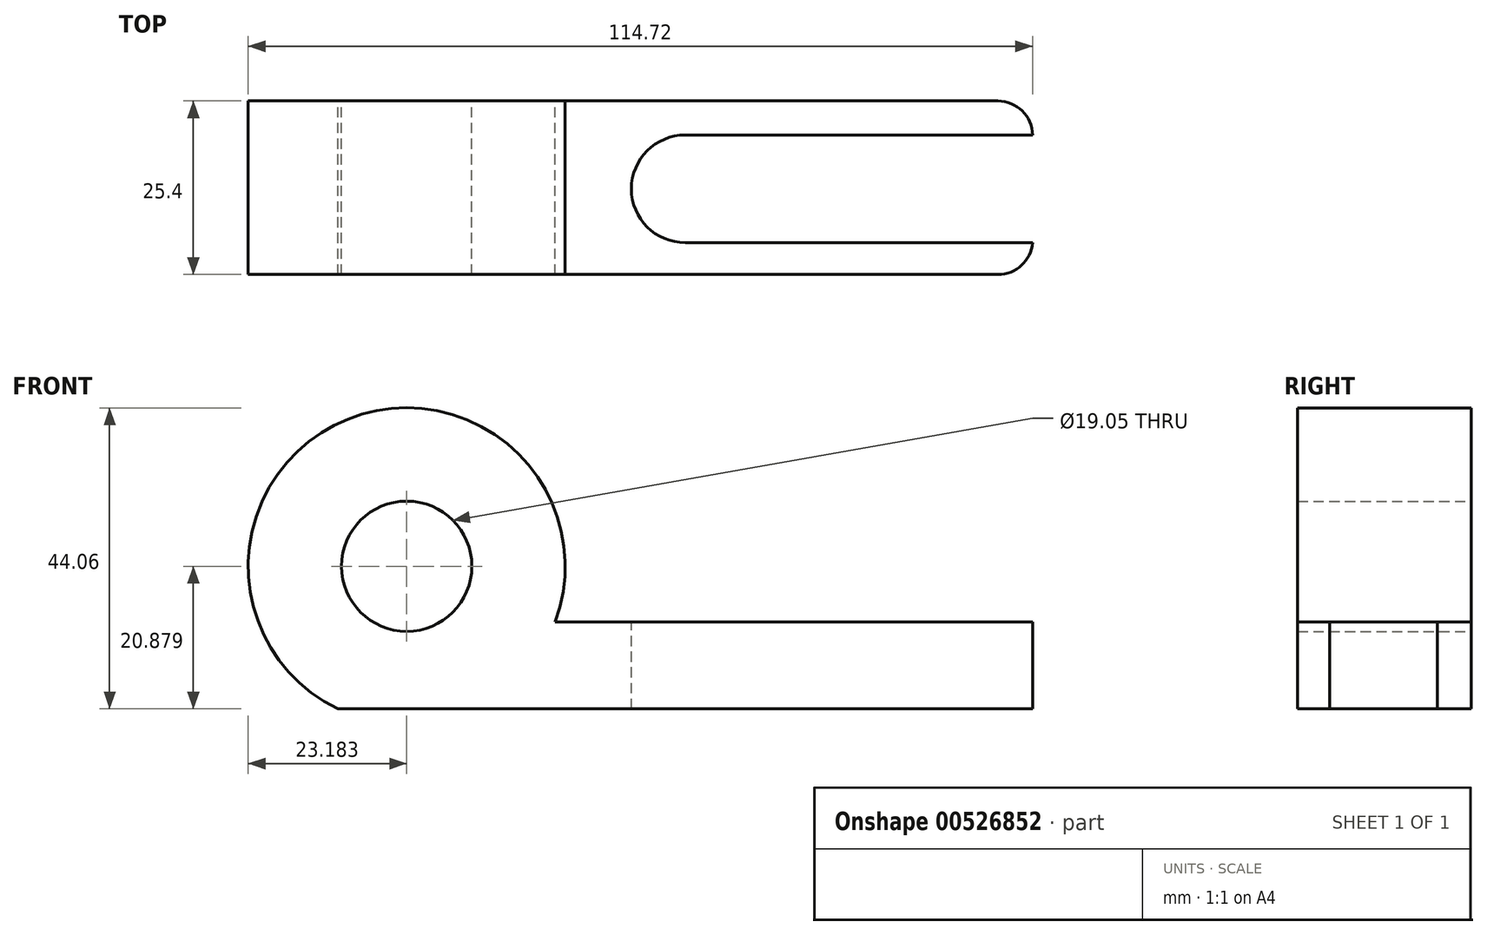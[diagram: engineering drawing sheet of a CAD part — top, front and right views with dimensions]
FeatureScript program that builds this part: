
annotation { "Feature Type Name" : "Feature", "Feature Type Description" : "" }
export const myFeature = defineFeature(function(context is Context, id is Id, definition is map)
    precondition{}
    {
        {
            var Q0;
            Q0=qCreatedBy(makeId("Front.planeOp"),FACE);
            var sketch = newSketch(context, id + "F0", { "sketchPlane" : qUnion([Q0])});
            skLineSegment(sketch, "E0", {"start": v(-52.73, 0) * mm, "end": v(48.87, 0) * mm});
            skLineSegment(sketch, "E1", {"start": v(48.87, 0) * mm, "end": v(48.87, 12.7) * mm});
            skLineSegment(sketch, "E2", {"start": v(48.87, 12.7) * mm, "end": v(-20.98, 12.7) * mm});
            skArc(sketch, "E3", {"start": v(-20.98, 12.7) * mm, "mid": v(-51.28, 42.4) * mm, "end": v(-52.73, 0) * mm});
            skCircle(sketch, "E4", {"center": v(-42.67, 20.88) * mm, "radius": 9.53 * mm});
            skSolve(sketch);
        }
        {
            var Q0;
            Q0=qCreatedBy(makeId("Right.planeOp"),FACE);
            var sketch = newSketch(context, id + "F1", { "sketchPlane" : qUnion([Q0])});
            skSolve(sketch);
        }
        {
            var Q0;
            Q0 = qSketchRegion(id + "F1", true);
            var Q1;
            Q1=makeQuery(id+"F0.imprint","IMPRINT",FACE,{"disambiguationData":[TD([[makeQuery(id+"F0.imprint","IMPRINT",EDGE,{"derivedFrom":sQuery(id+"F0.wireOp",EDGE,"E0")}),1.0]])]});
            extrude(context, id + "F2", {"entities" : qUnion([Q0, Q1]), "depth" : 25.4 * mm, "offsetDistance" : 25.4 * mm});
        }
        {
            var Q0;
            Q0=makeQuery(id+"F2.opExtrude","SWEPT_FACE",FACE,{"disambiguationData":[OSD([sQuery(id+"F0.wireOp",EDGE,"E2")])]});
            var sketch = newSketch(context, id + "F3", { "sketchPlane" : qUnion([Q0])});
            skLineSegment(sketch, "E5", {"start": v(48.87, -20.73) * mm, "end": v(-1.93, -20.73) * mm});
            skLineSegment(sketch, "E6", {"start": v(-1.93, -20.73) * mm, "end": v(-1.93, -4.98) * mm});
            skLineSegment(sketch, "E7", {"start": v(-1.93, -4.98) * mm, "end": v(48.87, -4.98) * mm});
            skLineSegment(sketch, "E8", {"start": v(48.87, -4.98) * mm, "end": v(48.87, -20.73) * mm});
            skArc(sketch, "E9", {"start": v(-1.93, -4.98) * mm, "mid": v(-9.8, -12.85) * mm, "end": v(-1.93, -20.73) * mm});
            skSolve(sketch);
        }
        {
            var Q0;
            Q0 = qSketchRegion(id + "F3", true);
            extrude(context, id + "F4", {"entities" : qUnion([Q0]), "operationType" : NewBodyOperationType.REMOVE, "oppositeDirection" : true, "depth" : 25.4 * mm, "offsetDistance" : 25.4 * mm});
        }
        {
            var Q0;
            Q0=makeQuery(id+"F2.opExtrude","CAP_EDGE",EDGE,{"disambiguationData":[OSD([sQuery(id+"F0.wireOp",EDGE,"E1")])],"isStart":true});
            var Q1;
            Q1=makeQuery(id+"F2.opExtrude","CAP_EDGE",EDGE,{"disambiguationData":[OSD([sQuery(id+"F0.wireOp",EDGE,"E1")])],"isStart":false});
            fillet(context, id + "F5", {"entities" : qUnion([Q0, Q1]), "radius" : 5.08 * mm, "tangentPropagation" : true, "allowEdgeOverflow" : false});
        }
    });
